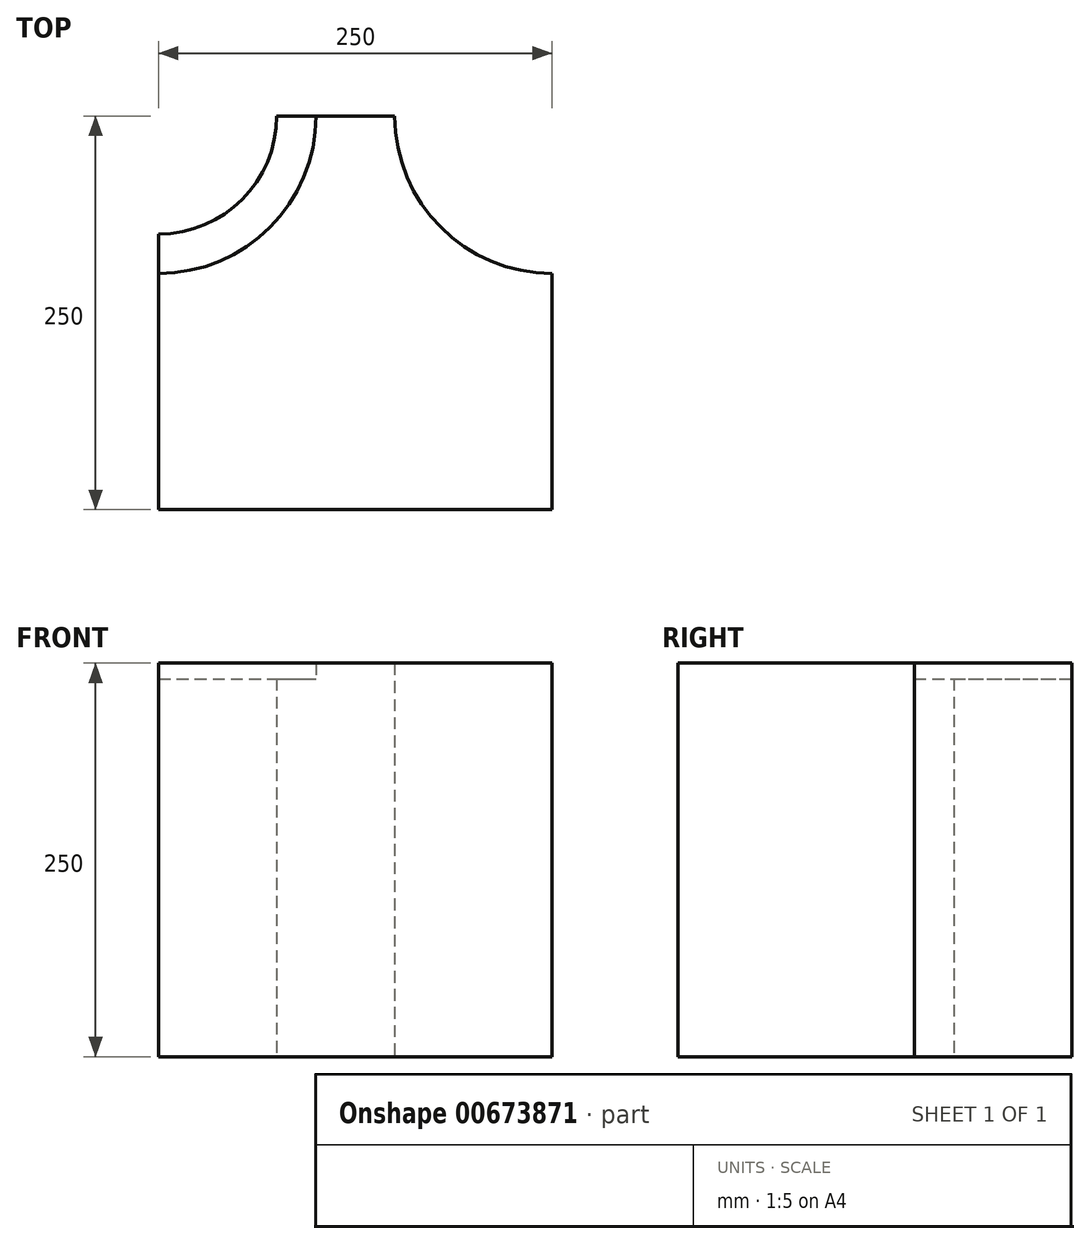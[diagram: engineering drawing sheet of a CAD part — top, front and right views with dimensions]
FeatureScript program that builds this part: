
annotation { "Feature Type Name" : "Feature", "Feature Type Description" : "" }
export const myFeature = defineFeature(function(context is Context, id is Id, definition is map)
    precondition{}
    {
        {
            var Q0;
            Q0=qCreatedBy(makeId("Top.planeOp"),FACE);
            var sketch = newSketch(context, id + "F0", { "sketchPlane" : qUnion([Q0])});
            skLineSegment(sketch, "E0", {"start": v(-118.75, -51.6) * mm, "end": v(-118.75, 48.4) * mm});
            skLineSegment(sketch, "E1", {"start": v(-43.75, 123.4) * mm, "end": v(56.25, 123.4) * mm});
            skLineSegment(sketch, "E2", {"start": v(131.25, -26.6) * mm, "end": v(131.25, 48.4) * mm});
            skLineSegment(sketch, "E3", {"start": v(31.25, -126.6) * mm, "end": v(-43.75, -126.6) * mm});
            skLineSegment(sketch, "E4", {"start": v(131.25, -26.6) * mm, "end": v(131.25, -51.6) * mm});
            skLineSegment(sketch, "E5", {"start": v(31.25, -126.6) * mm, "end": v(56.25, -126.6) * mm});
            skArc(sketch, "E6", {"start": v(-118.75, 48.4) * mm, "mid": v(-65.71, 70.37) * mm, "end": v(-43.75, 123.4) * mm});
            skLineSegment(sketch, "E7", {"start": v(-43.75, 123.4) * mm, "end": v(-18.75, 123.4) * mm});
            skLineSegment(sketch, "E8", {"start": v(-118.75, 48.4) * mm, "end": v(-118.75, 23.4) * mm});
            skArc(sketch, "E9", {"start": v(-118.75, 23.4) * mm, "mid": v(-48.04, 52.7) * mm, "end": v(-18.75, 123.4) * mm});
            skLineSegment(sketch, "E10", {"start": v(131.25, 48.4) * mm, "end": v(131.25, 23.4) * mm});
            skLineSegment(sketch, "E11", {"start": v(56.25, 123.4) * mm, "end": v(31.25, 123.4) * mm});
            skArc(sketch, "E12", {"start": v(56.25, 123.4) * mm, "mid": v(78.22, 70.37) * mm, "end": v(131.25, 48.4) * mm});
            skArc(sketch, "E13", {"start": v(31.25, 123.4) * mm, "mid": v(60.54, 52.7) * mm, "end": v(131.25, 23.4) * mm});
            skLineSegment(sketch, "E14", {"start": v(-118.75, -51.6) * mm, "end": v(-118.75, -26.6) * mm});
            skLineSegment(sketch, "E15", {"start": v(-43.75, -126.6) * mm, "end": v(-18.75, -126.6) * mm});
            skPoint(sketch, "E16.orphan", {"position": v(-118.75, -126.6) * mm});
            skLineSegment(sketch, "E17", {"start": v(-118.75, -51.6) * mm, "end": v(-118.75, -126.6) * mm});
            skLineSegment(sketch, "E18", {"start": v(-43.75, -126.6) * mm, "end": v(-118.75, -126.6) * mm});
            skLineSegment(sketch, "E19", {"start": v(131.25, -51.6) * mm, "end": v(131.25, -126.6) * mm});
            skLineSegment(sketch, "E20", {"start": v(56.25, -126.6) * mm, "end": v(131.25, -126.6) * mm});
            skSolve(sketch);
        }
        {
            var Q0;
            Q0=makeQuery(id+"F0.imprint","IMPRINT",FACE,{"disambiguationData":[TD([[makeQuery(id+"F0.imprint","IMPRINT",EDGE,{"derivedFrom":sQuery(id+"F0.wireOp",EDGE,"E0")}),-1.0]])]});
            extrude(context, id + "F1", {"entities" : qUnion([Q0]), "depth" : 250 * mm, "offsetDistance" : 25 * mm});
        }
        {
            var Q0;
            Q0=makeQuery(id+"F0.imprint","IMPRINT",FACE,{"disambiguationData":[TD([[makeQuery(id+"F0.imprint","IMPRINT",EDGE,{"derivedFrom":sQuery(id+"F0.wireOp",EDGE,"E6")}),-1.0]])]});
            var Q1;
            Q1=makeQuery(id+"F0.imprint","IMPRINT",FACE,{"disambiguationData":[TD([[makeQuery(id+"F0.imprint","IMPRINT",EDGE,{"derivedFrom":sQuery(id+"F0.wireOp",EDGE,"E10")}),-1.0]])]});
            extrude(context, id + "F2", {"entities" : qUnion([Q0, Q1]), "operationType" : NewBodyOperationType.ADD, "depth" : 240 * mm, "offsetDistance" : 25 * mm});
        }
    });
